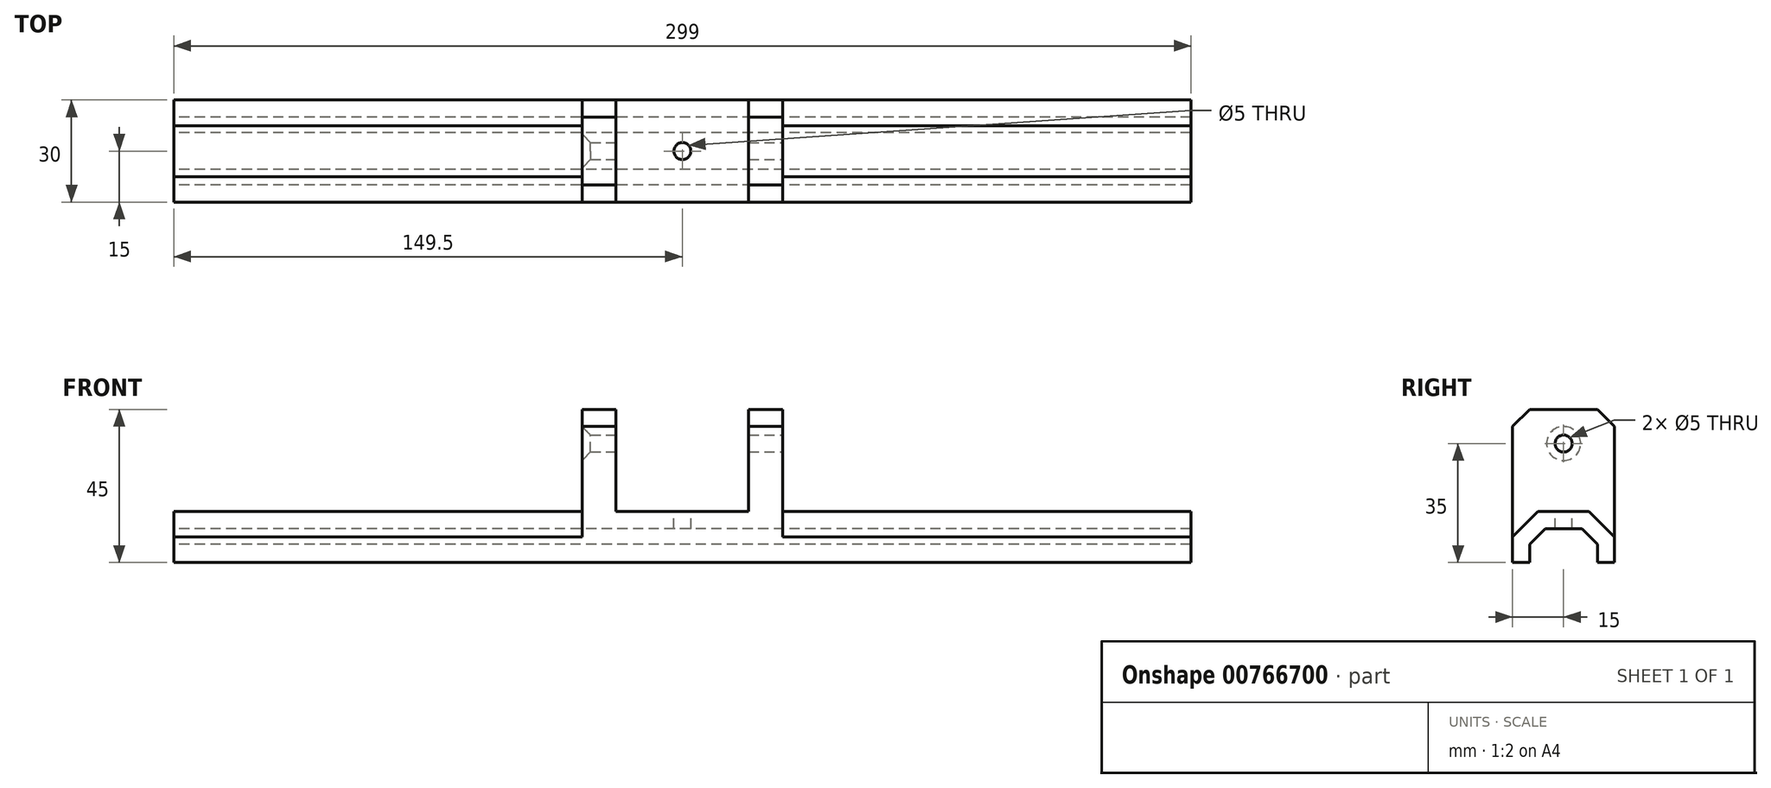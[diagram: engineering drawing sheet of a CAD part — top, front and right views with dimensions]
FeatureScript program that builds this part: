
annotation { "Feature Type Name" : "Feature", "Feature Type Description" : "" }
export const myFeature = defineFeature(function(context is Context, id is Id, definition is map)
    precondition{}
    {
        {
            var Q0;
            Q0=qCreatedBy(makeId("Front.planeOp"),FACE);
            var sketch = newSketch(context, id + "F0", { "sketchPlane" : qUnion([Q0])});
            skLineSegment(sketch, "E0", {"start": v(0, 0) * mm, "end": v(0, 100) * mm, "construction": true});
            skLineSegment(sketch, "E1", {"start": v(0, 0) * mm, "end": v(149.5, 0) * mm});
            skLineSegment(sketch, "E2", {"start": v(149.5, 0) * mm, "end": v(149.5, 15) * mm});
            skLineSegment(sketch, "E3", {"start": v(149.5, 15) * mm, "end": v(29.5, 15) * mm});
            skLineSegment(sketch, "E4", {"start": v(29.5, 15) * mm, "end": v(29.5, 45) * mm});
            skLineSegment(sketch, "E5", {"start": v(29.5, 45) * mm, "end": v(19.5, 45) * mm});
            skLineSegment(sketch, "E6", {"start": v(19.5, 45) * mm, "end": v(19.5, 15) * mm});
            skLineSegment(sketch, "E7", {"start": v(19.5, 15) * mm, "end": v(0, 15) * mm});
            skLineSegment(sketch, "E8.MirrorCS", {"start": v(0, 0) * mm, "end": v(-149.5, 0) * mm});
            skLineSegment(sketch, "E9.MirrorCS", {"start": v(-19.5, 15) * mm, "end": v(0, 15) * mm});
            skLineSegment(sketch, "E10.MirrorCS", {"start": v(-19.5, 45) * mm, "end": v(-19.5, 15) * mm});
            skLineSegment(sketch, "E11.MirrorCS", {"start": v(-149.5, 0) * mm, "end": v(-149.5, 15) * mm});
            skLineSegment(sketch, "E12.MirrorCS", {"start": v(-29.5, 15) * mm, "end": v(-29.5, 45) * mm});
            skLineSegment(sketch, "E13.MirrorCS", {"start": v(-29.5, 45) * mm, "end": v(-19.5, 45) * mm});
            skLineSegment(sketch, "E14.MirrorCS", {"start": v(-149.5, 15) * mm, "end": v(-29.5, 15) * mm});
            skSolve(sketch);
        }
        {
            var Q0;
            Q0=qSketchRegion(id+"F0",true);
            extrude(context, id + "F1", {"entities" : qUnion([Q0]), "depth" : 30 * mm, "offsetDistance" : 25 * mm});
        }
        {
            var Q0;
            Q0=makeQuery(id+"F1.opExtrude","CAP_EDGE",EDGE,{"disambiguationData":[OSD([sQuery(id+"F0.wireOp",EDGE,"E14.MirrorCS")])],"isStart":false});
            var Q1;
            Q1=makeQuery(id+"F1.opExtrude","CAP_EDGE",EDGE,{"disambiguationData":[OSD([sQuery(id+"F0.wireOp",EDGE,"E14.MirrorCS")])],"isStart":true});
            var Q2;
            Q2=makeQuery(id+"F1.opExtrude","CAP_EDGE",EDGE,{"disambiguationData":[OSD([sQuery(id+"F0.wireOp",EDGE,"E3")])],"isStart":true});
            var Q3;
            Q3=makeQuery(id+"F1.opExtrude","CAP_EDGE",EDGE,{"disambiguationData":[OSD([sQuery(id+"F0.wireOp",EDGE,"E3")])],"isStart":false});
            chamfer(context, id + "F2", {"entities" : qUnion([Q0, Q1, Q2, Q3]), "width" : 7.5 * mm, "tangentPropagation" : true});
        }
        {
            var Q0;
            Q0=makeQuery(id+"F1.opExtrude","SWEPT_FACE",FACE,{"disambiguationData":[OSD([sQuery(id+"F0.wireOp",EDGE,"E11.MirrorCS")])]});
            var sketch = newSketch(context, id + "F3", { "sketchPlane" : qUnion([Q0])});
            skLineSegment(sketch, "E15.0", {"start": v(5, 0) * mm, "end": v(5, 5.43) * mm});
            skLineSegment(sketch, "E15.1", {"start": v(25, 0) * mm, "end": v(25, 5.43) * mm});
            skLineSegment(sketch, "E15.2", {"start": v(25, 5.43) * mm, "end": v(20.43, 10) * mm});
            skLineSegment(sketch, "E15.3", {"start": v(20.43, 10) * mm, "end": v(9.57, 10) * mm});
            skLineSegment(sketch, "E15.4", {"start": v(9.57, 10) * mm, "end": v(5, 5.43) * mm});
            skLineSegment(sketch, "E16", {"start": v(0, 0) * mm, "end": v(5, 0) * mm});
            skLineSegment(sketch, "E17", {"start": v(25, 0) * mm, "end": v(30, 0) * mm});
            skSolve(sketch);
        }
        {
            var Q0;
            {var subQ1=sQuery(id+"F3.wireOp",EDGE,"E15.0");Q0=makeQuery(id+"F3.imprint","IMPRINT",FACE,{"disambiguationData":[TD([[makeQuery(id+"F3.imprint","IMPRINT",EDGE,{"derivedFrom":subQ1}),-1.0]])]});}
            extrude(context, id + "F4", {"entities" : qUnion([Q0]), "operationType" : NewBodyOperationType.REMOVE, "endBound" : BoundingType.THROUGH_ALL, "oppositeDirection" : true, "depth" : 25 * mm, "offsetDistance" : 25 * mm});
        }
        {
            var Q0;
            Q0=makeQuery(id+"F1.opExtrude","CAP_EDGE",EDGE,{"disambiguationData":[OSD([sQuery(id+"F0.wireOp",EDGE,"E13.MirrorCS")])],"isStart":true});
            var Q1;
            Q1=makeQuery(id+"F1.opExtrude","CAP_EDGE",EDGE,{"disambiguationData":[OSD([sQuery(id+"F0.wireOp",EDGE,"E13.MirrorCS")])],"isStart":false});
            var Q2;
            Q2=makeQuery(id+"F1.opExtrude","CAP_EDGE",EDGE,{"disambiguationData":[OSD([sQuery(id+"F0.wireOp",EDGE,"E5")])],"isStart":true});
            var Q3;
            Q3=makeQuery(id+"F1.opExtrude","CAP_EDGE",EDGE,{"disambiguationData":[OSD([sQuery(id+"F0.wireOp",EDGE,"E5")])],"isStart":false});
            chamfer(context, id + "F5", {"entities" : qUnion([Q0, Q1, Q2, Q3]), "width" : 5 * mm, "tangentPropagation" : true});
        }
        {
            var Q0;
            Q0=makeQuery(id+"F1.opExtrude","SWEPT_FACE",FACE,{"disambiguationData":[OSD([sQuery(id+"F0.wireOp",EDGE,"E4")])]});
            var sketch = newSketch(context, id + "F6", { "sketchPlane" : qUnion([Q0])});
            skCircle(sketch, "E18", {"center": v(-15, 35) * mm, "radius": 2.5 * mm});
            skPoint(sketch, "E18.centerSnap0", {"position": v(-15, 45) * mm});
            skSolve(sketch);
        }
        {
            var Q0;
            Q0=qSketchRegion(id+"F6",true);
            extrude(context, id + "F7", {"entities" : qUnion([Q0]), "operationType" : NewBodyOperationType.REMOVE, "endBound" : BoundingType.THROUGH_ALL, "oppositeDirection" : true, "depth" : 25 * mm, "offsetDistance" : 25 * mm});
        }
        {
            var Q0;
            Q0=makeQuery(id+"F1.opExtrude","SWEPT_FACE",FACE,{"disambiguationData":[OSD([sQuery(id+"F0.wireOp",EDGE,"E7"),sQuery(id+"F0.wireOp",EDGE,"E9.MirrorCS")])]});
            var sketch = newSketch(context, id + "F8", { "sketchPlane" : qUnion([Q0])});
            skCircle(sketch, "E19", {"center": v(0, -15) * mm, "radius": 2.5 * mm});
            skPoint(sketch, "E19.centerSnap0", {"position": v(19.5, -15) * mm});
            skSolve(sketch);
        }
        {
            var Q0;
            Q0=qSketchRegion(id+"F8",true);
            extrude(context, id + "F9", {"entities" : qUnion([Q0]), "operationType" : NewBodyOperationType.REMOVE, "endBound" : BoundingType.THROUGH_ALL, "oppositeDirection" : true, "depth" : 25 * mm, "offsetDistance" : 25 * mm});
        }
        {
            var Q0;
            {var subQ6=sQuery(id+"F0.wireOp",EDGE,"E8.MirrorCS");var subQ13=sQuery(id+"F0.wireOp",EDGE,"E1");var subQ16=makeQuery(id+"F1.opExtrude","SWEPT_FACE",FACE,{"disambiguationData":[OSD([subQ13,subQ6])]});Q0=makeQuery(id+"F9.boolean.opBoolean","INTERSECT",EDGE,{"derivedFrom":[makeQuery(id+"F5krsDRfj2hvqP5_1.boolean.opBoolean","MERGE",FACE,{"derivedFrom":[makeQuery(id+"F4.boolean.opBoolean","SPLIT",FACE,{"disambiguationData":[TD([makeQuery(id+"F4.opExtrude","SWEPT_FACE",FACE,{"disambiguationData":[OSD([sQuery(id+"F3.wireOp",EDGE,"j8OshkOk-lQh9-liAU-tSGP-X9TM9vxK6T69.left")])]})])],"derivedFrom":subQ16}),makeQuery(id+"F4.boolean.opBoolean","SPLIT",FACE,{"disambiguationData":[TD([makeQuery(id+"F4.opExtrude","SWEPT_FACE",FACE,{"disambiguationData":[OSD([sQuery(id+"F3.wireOp",EDGE,"j8OshkOk-lQh9-liAU-tSGP-X9TM9vxK6T69.right")])]})])],"derivedFrom":subQ16}),makeQuery(id+"F5krsDRfj2hvqP5_1.opExtrude","CAP_FACE",FACE,{"disambiguationData":[OSD([sQuery(id+"FMAmxCnodQVa9ww_1.wireOp",EDGE,"OFStoJCs-5hsC-Rgwx-D28J-JvS6MQ9GuzZL.bottom"),sQuery(id+"FMAmxCnodQVa9ww_1.wireOp",EDGE,"OFStoJCs-5hsC-Rgwx-D28J-JvS6MQ9GuzZL.top"),sQuery(id+"FMAmxCnodQVa9ww_1.wireOp",EDGE,"OFStoJCs-5hsC-Rgwx-D28J-JvS6MQ9GuzZL.left"),sQuery(id+"FMAmxCnodQVa9ww_1.wireOp",EDGE,"OFStoJCs-5hsC-Rgwx-D28J-JvS6MQ9GuzZL.right")])],"isStart":true})]}),makeQuery(id+"F9.opExtrude","SWEPT_FACE",FACE,{"disambiguationData":[OSD([sQuery(id+"F8.wireOp",EDGE,"E19")])]})]});}
            var Q1;
            Q1=makeQuery(id+"F7.boolean.opBoolean","INTERSECT",EDGE,{"derivedFrom":[makeQuery(id+"F1.opExtrude","SWEPT_FACE",FACE,{"disambiguationData":[OSD([sQuery(id+"F0.wireOp",EDGE,"E12.MirrorCS")])]}),makeQuery(id+"F7.opExtrude","SWEPT_FACE",FACE,{"disambiguationData":[OSD([sQuery(id+"F6.wireOp",EDGE,"E18")])]})]});
            var Q2;
            Q2=makeQuery(id+"F7.boolean.opBoolean","COPY",EDGE,{"derivedFrom":makeQuery(id+"F7.opExtrude","CAP_EDGE",EDGE,{"disambiguationData":[OSD([sQuery(id+"F6.wireOp",EDGE,"E18")])],"isStart":true})});
            chamfer(context, id + "F10", {"entities" : qUnion([Q0, Q1, Q2]), "width" : 2.5 * mm, "tangentPropagation" : true});
        }
    });
